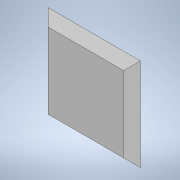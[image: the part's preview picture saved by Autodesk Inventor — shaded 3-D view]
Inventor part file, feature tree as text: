
AUTODESK INVENTOR PART (.ipt)
format: ipt  version: 2021 (Build 250183000, 183)  size: 93,696 bytes
history: native  units: in
note: dims shown in document units (in); Inventor stores cm internally (conversion verified against a paired STEP export)
features: extrude x1, chamfer x1, sketch x1
ambient origin geometry x8: Origin, YZ Plane, XZ Plane, XY Plane, X Axis, Y Axis, Z Axis, Center Point
bodies: Solid1 (feature_tree)
feature tree (3):
  extrude  "Extrusion1"  Depth=0.1575in
  chamfer  "Chamfer1"  Distance=0.1575in
  sketch  "Sketch1"  dims[d0=1.7323in d1=1.7323in d2=0.1575in d3=0.0in d4=0.1575in d5=0.0787in d6=45.0deg]
